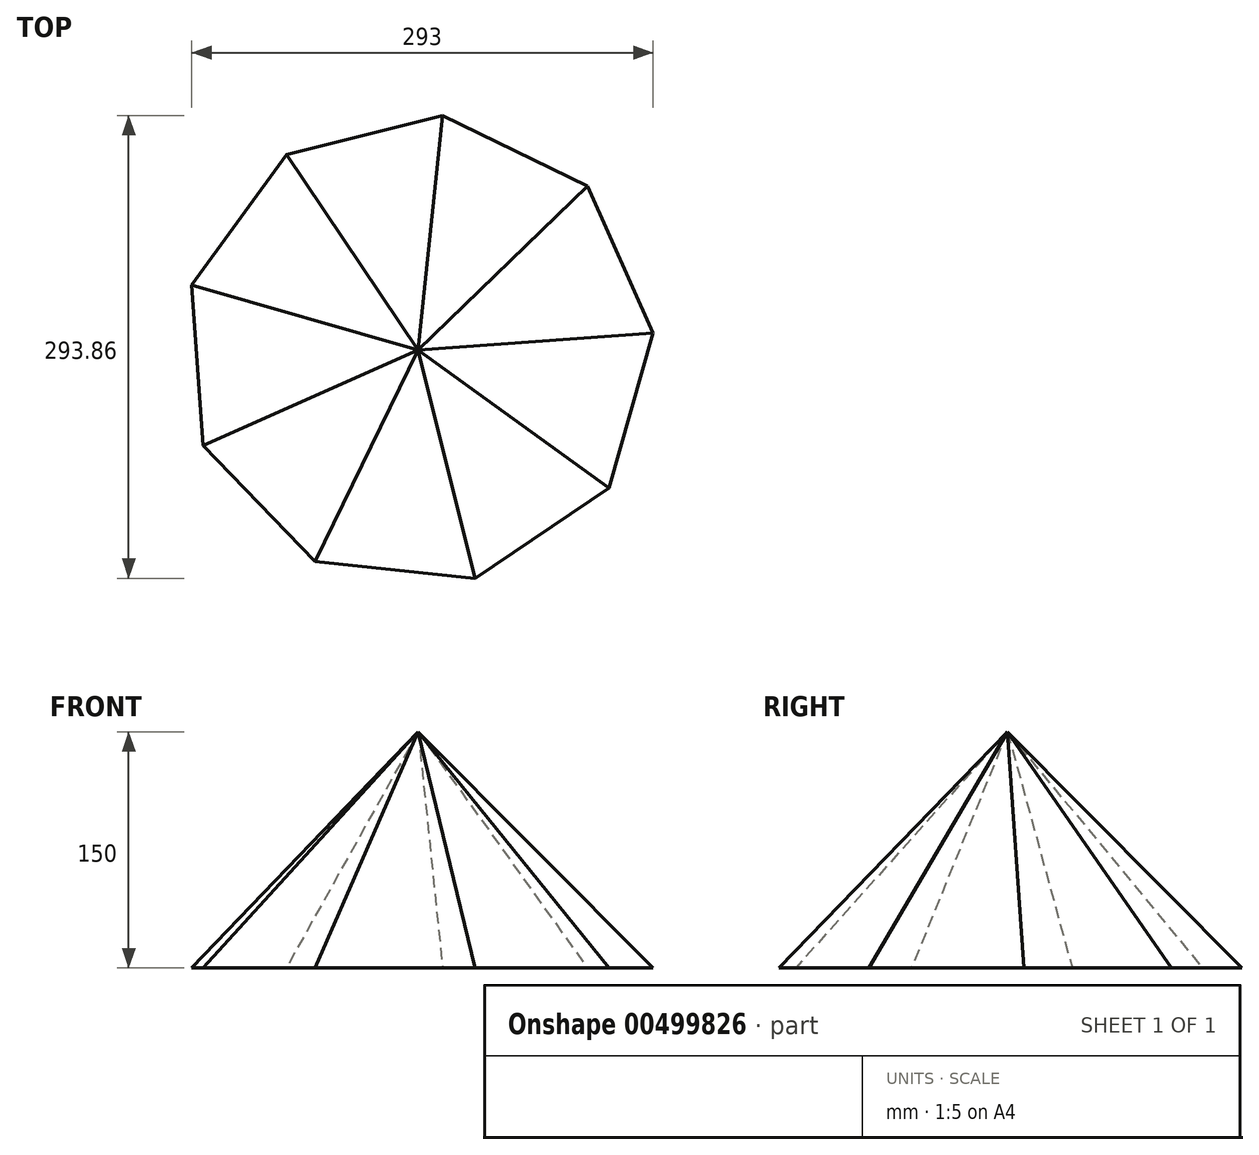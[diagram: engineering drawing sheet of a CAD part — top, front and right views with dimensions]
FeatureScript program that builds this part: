
annotation { "Feature Type Name" : "Feature", "Feature Type Description" : "" }
export const myFeature = defineFeature(function(context is Context, id is Id, definition is map)
    precondition{}
    {
        {
            var Q0;
            Q0=qCreatedBy(makeId("Top.planeOp"),FACE);
            var sketch = newSketch(context, id + "F0", { "sketchPlane" : qUnion([Q0])});
            skCircle(sketch, "E0.cCircle", {"center": v(0, 0) * mm, "radius": 149.57 * mm, "construction": true});
            skLineSegment(sketch, "E0.0", {"start": v(15.54, 148.76) * mm, "end": v(107.53, 103.97) * mm});
            skLineSegment(sketch, "E0.1", {"start": v(107.53, 103.97) * mm, "end": v(149.2, 10.53) * mm});
            skLineSegment(sketch, "E0.2", {"start": v(149.2, 10.53) * mm, "end": v(121.06, -87.84) * mm});
            skLineSegment(sketch, "E0.3", {"start": v(121.06, -87.84) * mm, "end": v(36.28, -145.1) * mm});
            skLineSegment(sketch, "E0.4", {"start": v(36.28, -145.1) * mm, "end": v(-65.48, -134.48) * mm});
            skLineSegment(sketch, "E0.5", {"start": v(-65.48, -134.48) * mm, "end": v(-136.6, -60.92) * mm});
            skLineSegment(sketch, "E0.6", {"start": v(-136.6, -60.92) * mm, "end": v(-143.8, 41.14) * mm});
            skLineSegment(sketch, "E0.7", {"start": v(-143.8, 41.14) * mm, "end": v(-83.72, 123.95) * mm});
            skLineSegment(sketch, "E0.8", {"start": v(-83.72, 123.95) * mm, "end": v(15.54, 148.76) * mm});
            skSolve(sketch);
        }
        {
            var Q0;
            Q0=qCreatedBy(makeId("Top.planeOp"),FACE);
            cPlane(context, id + "F1", {"entities" : qUnion([Q0]), "cplaneType" : CPlaneType.OFFSET, "offset" : 150 * mm, "width" : 150 * mm, "height" : 150 * mm});
        }
        {
            var Q0;
            Q0=qCreatedBy(id+"F1.planeOp",FACE);
            var sketch = newSketch(context, id + "F2", { "sketchPlane" : qUnion([Q0])});
            skPoint(sketch, "E1", {"position": v(0, 0) * mm});
            skSolve(sketch);
        }
        {
            var Q0;
            Q0=sQuery(id+"F2.wireOp",VERTEX,"E1");
            var Q1;
            Q1=makeQuery(id+"F0.imprint","IMPRINT",FACE,{"disambiguationData":[TD([[makeQuery(id+"F0.imprint","IMPRINT",EDGE,{"derivedFrom":sQuery(id+"F0.wireOp",EDGE,"E0.0")}),-1.0]])]});
            loft(context, id + "F3", {"sheetProfilesArray" : [{ "sheetProfileEntities" : qUnion([Q0]) }, { "sheetProfileEntities" : qUnion([Q1]) }]});
        }
    });
